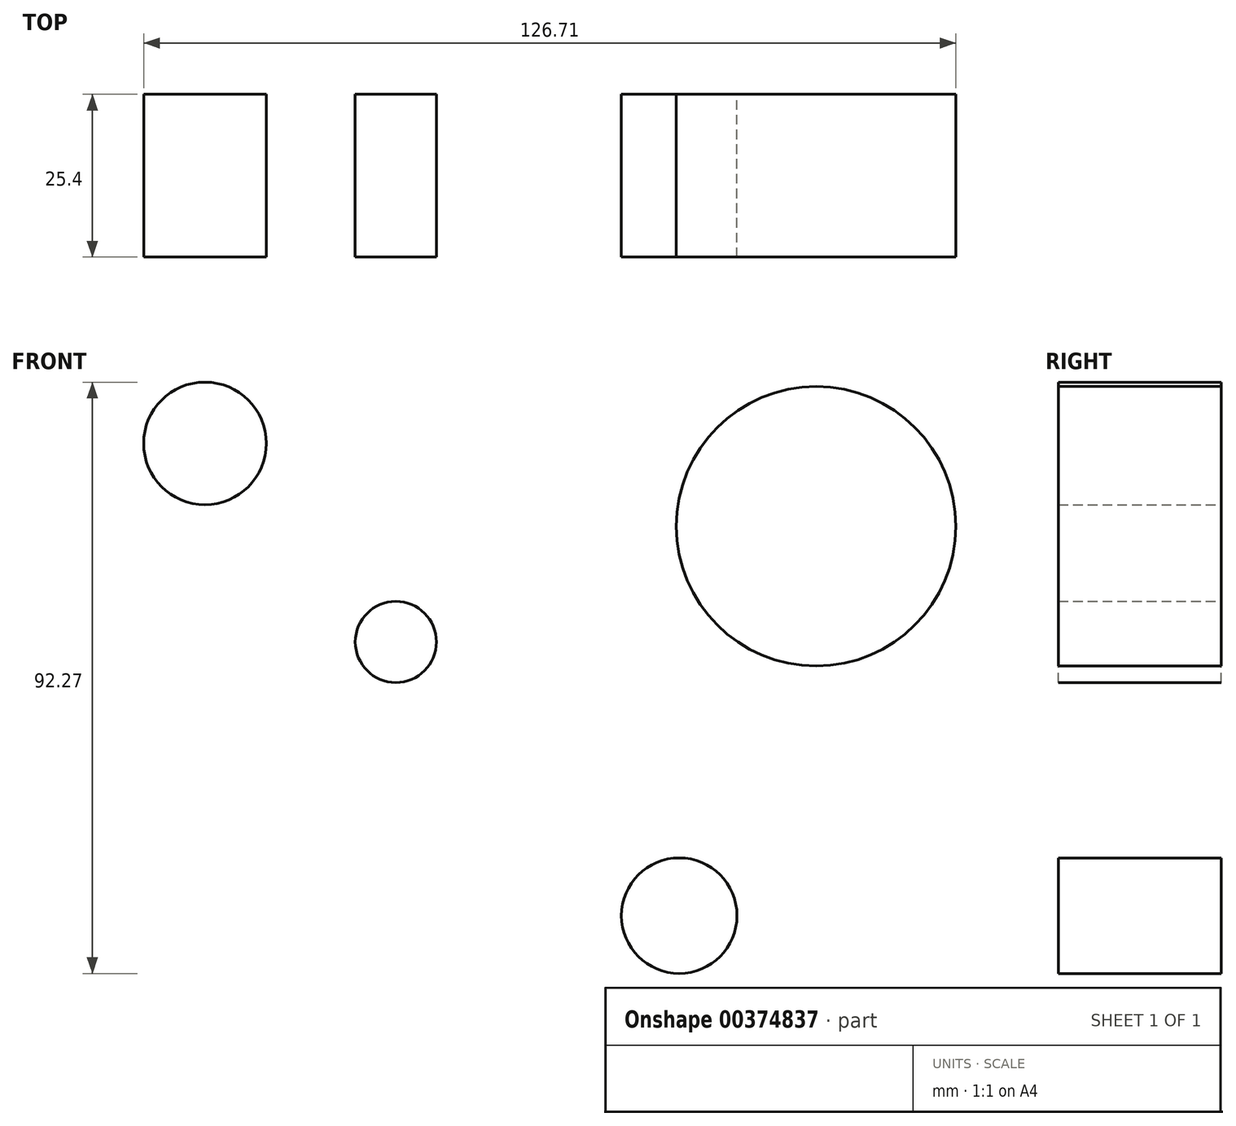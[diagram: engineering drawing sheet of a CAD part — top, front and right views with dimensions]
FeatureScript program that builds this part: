
annotation { "Feature Type Name" : "Feature", "Feature Type Description" : "" }
export const myFeature = defineFeature(function(context is Context, id is Id, definition is map)
    precondition{}
    {
        {
            var Q0;
            Q0=qCreatedBy(makeId("Front.planeOp"),FACE);
            var sketch = newSketch(context, id + "F0", { "sketchPlane" : qUnion([Q0])});
            skCircle(sketch, "E0", {"center": v(-108.89, 27.07) * mm, "radius": 9.56 * mm});
            skCircle(sketch, "E1", {"center": v(-13.54, 14.14) * mm, "radius": 21.8 * mm});
            skCircle(sketch, "E2", {"center": v(-34.9, -46.62) * mm, "radius": 9.01 * mm});
            skCircle(sketch, "E3", {"center": v(-79.1, -3.91) * mm, "radius": 6.32 * mm});
            skSolve(sketch);
        }
        {
            var Q0;
            Q0 = qSketchRegion(id + "F0", true);
            extrude(context, id + "F1", {"entities" : qUnion([Q0]), "endBound" : BoundingType.SYMMETRIC, "depth" : 25.4 * mm});
        }
    });
